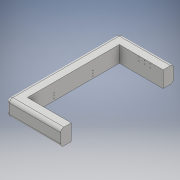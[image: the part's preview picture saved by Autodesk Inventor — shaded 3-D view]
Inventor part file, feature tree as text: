
AUTODESK INVENTOR PART (.ipt)
format: ipt  version: 2018 (Build 220112000, 112)  size: 178,176 bytes
history: native  units: in
note: dims shown in document units (in); Inventor stores cm internally (conversion verified against a paired STEP export)
features: extrude x4, sketch x4, fillet x1
ambient origin geometry x8: Origin, YZ Plane, XZ Plane, XY Plane, X Axis, Y Axis, Z Axis, Center Point
bodies: Solid1 (feature_tree)
feature tree (9):
  extrude  "Extrusion1"  Depth=13.5in
  fillet  "Fillet1"  Radius=3.25in
  extrude  "Extrusion2"  Depth=1.0in
  extrude  "Extrusion3"  Depth=1.75in
  extrude  "Extrusion4"  Depth=0.1875in
  sketch  "Sketch1"  dims[d0=28.31in d1=13.5in d2=3.25in]
  sketch  "Sketch2"  dims[d3=5.0in d4=0.0in d5=1.0in]
  sketch  "Sketch3"  dims[d7=4.0in d8=1.75in]
  sketch  "Sketch4"  dims[d9=1.75in d10=0.375in d11=1.0in d12=0.21in d13=0.1875in d14=0.0in d15=0.375in d16=4.0in d17=1.75in d18=1.75in d19=1.0in d20=0.21in d21=0.1875in d22=0.0in d23=8.155in d24=2.83in d25=0.75in d26=0.75in d27=0.21in d28=0.1875in d29=0.0in]
